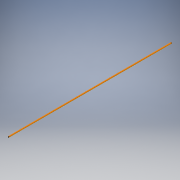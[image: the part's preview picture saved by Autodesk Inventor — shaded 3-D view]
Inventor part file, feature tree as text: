
AUTODESK INVENTOR PART (.ipt)
format: ipt  version: 2017 (Build 210142000, 142)  size: 109,568 bytes
history: native  units: in
note: dims shown in document units (in); Inventor stores cm internally (conversion verified against a paired STEP export)
features: sketch x2, extrude x1, hole x1
ambient origin geometry x8: Origin, YZ Plane, XZ Plane, XY Plane, X Axis, Y Axis, Z Axis, Center Point
bodies: Solid1 (feature_tree)
feature tree (4):
  extrude  "Extrusion1"  Depth=0.3937in
  hole  "Hole1"  [1 undecoded]
  sketch  "Sketch1"  dims[d0=0.3937in d1=0.1575in]
  sketch  "Sketch2"  dims[d2=0.0787in d3=0.0787in d4=59.0551in d5=0.0in d6=0.0709in d7=0.2362in d8=0.1575in d9=0.0787in d10=90.0deg d11=0.0787in d12=0.8108in]
note: 1 required parameter value undecoded (feature->parameter linkage not recoverable at this tier; creation-order binding heuristic only, values carry confidence <= 0.55)
